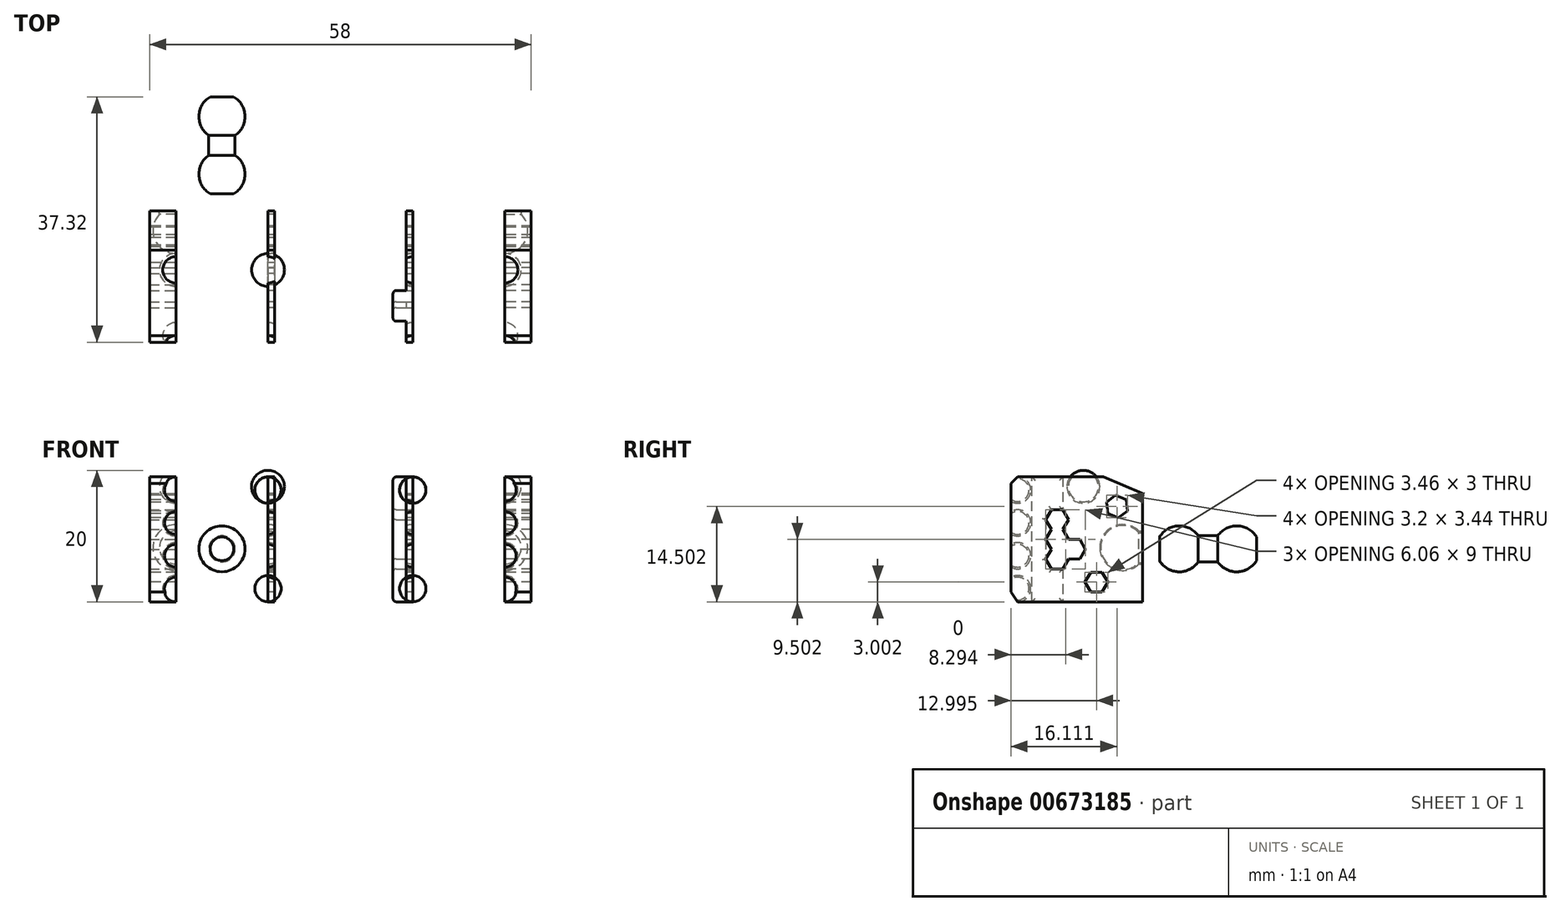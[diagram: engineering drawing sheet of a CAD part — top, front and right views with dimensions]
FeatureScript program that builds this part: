
annotation { "Feature Type Name" : "Feature", "Feature Type Description" : "" }
export const myFeature = defineFeature(function(context is Context, id is Id, definition is map)
    precondition{}
    {
        {
            var Q0;
            Q0=qCreatedBy(makeId("Right.planeOp"),FACE);
            var sketch = newSketch(context, id + "F0", { "sketchPlane" : qUnion([Q0])});
            skPoint(sketch, "E0.startSnap0", {"position": v(7.18, 6.6) * mm});
            skLineSegment(sketch, "E1", {"start": v(7.18, -0.9) * mm, "end": v(-7.82, -0.9) * mm});
            skLineSegment(sketch, "E2", {"start": v(-0.32, 14.1) * mm, "end": v(-0.32, 15.6) * mm, "construction": true});
            skPoint(sketch, "E2.endSnap0", {"position": v(-0.32, 14.1) * mm});
            skLineSegment(sketch, "E3", {"start": v(-4.07, 15.6) * mm, "end": v(-4.27, 15.6) * mm});
            skLineSegment(sketch, "E4", {"start": v(-7.82, 15.6) * mm, "end": v(-7.82, -0.9) * mm});
            skPoint(sketch, "E5.centerSnap0", {"position": v(-4.07, 15.6) * mm});
            skLineSegment(sketch, "E6.bottom", {"start": v(-7.82, 15.6) * mm, "end": v(-12.82, 15.6) * mm});
            skLineSegment(sketch, "E6.top", {"start": v(-7.82, -0.9) * mm, "end": v(-12.82, -0.9) * mm});
            skLineSegment(sketch, "E6.right", {"start": v(-12.82, 15.6) * mm, "end": v(-12.82, -0.9) * mm});
            skArc(sketch, "E7", {"start": v(-13.82, 14.6) * mm, "mid": v(-11.82, 12.6) * mm, "end": v(-9.82, 14.6) * mm});
            skArc(sketch, "E8.1.0.0", {"start": v(-13.82, 9.6) * mm, "mid": v(-11.82, 7.6) * mm, "end": v(-9.82, 9.6) * mm});
            skArc(sketch, "E8.2.0.0", {"start": v(-13.82, 4.6) * mm, "mid": v(-11.82, 2.6) * mm, "end": v(-9.82, 4.6) * mm});
            skArc(sketch, "E8.3.0.0", {"start": v(-13.82, -0.4) * mm, "mid": v(-11.82, -2.4) * mm, "end": v(-9.82, -0.4) * mm});
            skLineSegment(sketch, "E8.direction1", {"start": v(-11.82, 14.6) * mm, "end": v(-11.82, 9.6) * mm, "construction": true});
            skArc(sketch, "E9", {"start": v(-4.32, 15.1) * mm, "mid": v(-1.82, 12.6) * mm, "end": v(0.68, 15.1) * mm});
            skLineSegment(sketch, "E10", {"start": v(-11.82, -2.4) * mm, "end": v(7.18, -2.4) * mm});
            skLineSegment(sketch, "E11", {"start": v(-11.82, 16.6) * mm, "end": v(1.18, 16.6) * mm});
            skLineSegment(sketch, "E12", {"start": v(1.18, 16.6) * mm, "end": v(7.18, 14.1) * mm});
            skLineSegment(sketch, "E13", {"start": v(7.18, 14.1) * mm, "end": v(7.18, -2.4) * mm});
            skLineSegment(sketch, "E14", {"start": v(-12.82, -0.9) * mm, "end": v(-11.82, -2.4) * mm});
            skLineSegment(sketch, "E15", {"start": v(-11.82, 16.6) * mm, "end": v(-12.82, 15.6) * mm});
            skLineSegment(sketch, "E16", {"start": v(-13.82, -0.4) * mm, "end": v(-9.82, -0.4) * mm});
            skLineSegment(sketch, "E17", {"start": v(-9.82, 4.6) * mm, "end": v(-13.82, 4.6) * mm});
            skLineSegment(sketch, "E18", {"start": v(-9.82, 9.6) * mm, "end": v(-13.82, 9.6) * mm});
            skLineSegment(sketch, "E19", {"start": v(-9.82, 14.6) * mm, "end": v(-13.82, 14.6) * mm});
            skLineSegment(sketch, "E20", {"start": v(0.68, 15.1) * mm, "end": v(-4.32, 15.1) * mm});
            skArc(sketch, "E21", {"start": v(0.68, 5.85) * mm, "mid": v(2.82, 2.62) * mm, "end": v(6.62, 3.35) * mm});
            skPoint(sketch, "E21.centerSnap0", {"position": v(7.18, 5.85) * mm});
            skLineSegment(sketch, "E22", {"start": v(0.68, 5.85) * mm, "end": v(7.68, 5.85) * mm});
            skLineSegment(sketch, "E23", {"start": v(7.68, 5.85) * mm, "end": v(7.68, 3.35) * mm, "construction": true});
            skLineSegment(sketch, "E24", {"start": v(7.18, 3.35) * mm, "end": v(6.62, 3.35) * mm});
            skSolve(sketch);
        }
        {
            var Q0;
            {var subQ0=sQuery(id+"F0.wireOp",EDGE,"E8.1.0.0");var subQ1=sQuery(id+"F0.wireOp",EDGE,"E6.right");var subQ2=makeQuery(id+"F0.imprint","INTERSECT",VERTEX,{"disambiguationData":[OD(0.0)],"derivedFrom":[subQ1,subQ0]});Q0=makeQuery(id+"F0.imprint","IMPRINT",FACE,{"disambiguationData":[TD([[makeQuery(id+"F0.imprint","IMPRINT",EDGE,{"disambiguationData":[TD([[subQ2,-1.0]])],"derivedFrom":subQ1}),1.0]])]});}
            var Q1;
            {var subQ0=sQuery(id+"F0.wireOp",EDGE,"E8.2.0.0");var subQ1=sQuery(id+"F0.wireOp",EDGE,"E6.right");var subQ2=makeQuery(id+"F0.imprint","INTERSECT",VERTEX,{"disambiguationData":[OD(0.0)],"derivedFrom":[subQ1,subQ0]});Q1=makeQuery(id+"F0.imprint","IMPRINT",FACE,{"disambiguationData":[TD([[makeQuery(id+"F0.imprint","IMPRINT",EDGE,{"disambiguationData":[TD([[subQ2,-1.0]])],"derivedFrom":subQ1}),1.0]])]});}
            var Q2;
            {var subQ0=sQuery(id+"F0.wireOp",EDGE,"E9");var subQ1=makeQuery(id+"F0.imprint","IMPRINT",VERTEX,{"derivedFrom":subQ0});Q2=makeQuery(id+"F0.imprint","IMPRINT",FACE,{"disambiguationData":[TD([[makeQuery(id+"F0.imprint","IMPRINT",EDGE,{"disambiguationData":[TD([[subQ1,1.0]])],"derivedFrom":subQ0}),1.0]])]});}
            var Q3;
            {var subQ5=sQuery(id+"F0.wireOp",EDGE,"E1");Q3=makeQuery(id+"F0.imprint","IMPRINT",FACE,{"disambiguationData":[TD([[makeQuery(id+"F0.imprint","IMPRINT",EDGE,{"derivedFrom":subQ5}),1.0]])]});}
            var Q4;
            {var subQ0=sQuery(id+"F0.wireOp",EDGE,"E6.right");var subQ3=sQuery(id+"F0.wireOp",EDGE,"E7");var subQ5=makeQuery(id+"F0.imprint","INTERSECT",VERTEX,{"derivedFrom":[subQ0,subQ3]});Q4=makeQuery(id+"F0.imprint","IMPRINT",FACE,{"disambiguationData":[TD([[makeQuery(id+"F0.imprint","IMPRINT",EDGE,{"disambiguationData":[TD([[subQ5,-1.0]])],"derivedFrom":subQ3}),1.0]])]});}
            var Q5;
            {var subQ0=sQuery(id+"F0.wireOp",EDGE,"E15");Q5=makeQuery(id+"F0.imprint","IMPRINT",FACE,{"disambiguationData":[TD([[makeQuery(id+"F0.imprint","IMPRINT",EDGE,{"derivedFrom":subQ0}),1.0]])]});}
            var Q6;
            {var subQ0=sQuery(id+"F0.wireOp",EDGE,"E6.right");var subQ3=sQuery(id+"F0.wireOp",EDGE,"E8.3.0.0");var subQ5=makeQuery(id+"F0.imprint","INTERSECT",VERTEX,{"derivedFrom":[subQ0,subQ3]});Q6=makeQuery(id+"F0.imprint","IMPRINT",FACE,{"disambiguationData":[TD([[makeQuery(id+"F0.imprint","IMPRINT",EDGE,{"disambiguationData":[TD([[subQ5,1.0]])],"derivedFrom":subQ3}),1.0]])]});}
            var Q7;
            {var subQ0=sQuery(id+"F0.wireOp",EDGE,"E14");Q7=makeQuery(id+"F0.imprint","IMPRINT",FACE,{"disambiguationData":[TD([[makeQuery(id+"F0.imprint","IMPRINT",EDGE,{"derivedFrom":subQ0}),1.0]])]});}
            var Q8;
            {var subQ9=sQuery(id+"F0.wireOp",EDGE,"E1");Q8=makeQuery(id+"F0.imprint","IMPRINT",FACE,{"disambiguationData":[TD([[makeQuery(id+"F0.imprint","IMPRINT",EDGE,{"derivedFrom":subQ9}),-1.0]])]});}
            var Q9;
            {var subQ5=sQuery(id+"F0.wireOp",EDGE,"E4");Q9=makeQuery(id+"F0.imprint","IMPRINT",FACE,{"disambiguationData":[TD([[makeQuery(id+"F0.imprint","IMPRINT",EDGE,{"derivedFrom":subQ5}),-1.0]])]});}
            var Q10;
            {var subQ0=sQuery(id+"F0.wireOp",EDGE,"E18");var subQ1=sQuery(id+"F0.wireOp",EDGE,"E6.right");var subQ2=makeQuery(id+"F0.imprint","INTERSECT",VERTEX,{"derivedFrom":[subQ1,subQ0]});Q10=makeQuery(id+"F0.imprint","IMPRINT",FACE,{"disambiguationData":[TD([[makeQuery(id+"F0.imprint","IMPRINT",EDGE,{"disambiguationData":[TD([[subQ2,-1.0]])],"derivedFrom":subQ1}),1.0]])]});}
            var Q11;
            {var subQ0=sQuery(id+"F0.wireOp",EDGE,"E17");var subQ1=sQuery(id+"F0.wireOp",EDGE,"E6.right");var subQ2=makeQuery(id+"F0.imprint","INTERSECT",VERTEX,{"derivedFrom":[subQ1,subQ0]});Q11=makeQuery(id+"F0.imprint","IMPRINT",FACE,{"disambiguationData":[TD([[makeQuery(id+"F0.imprint","IMPRINT",EDGE,{"disambiguationData":[TD([[subQ2,-1.0]])],"derivedFrom":subQ1}),1.0]])]});}
            var Q12;
            Q12=makeQuery(id+"F0.imprint","IMPRINT",FACE,{"disambiguationData":[TD([[makeQuery(id+"F0.imprint","IMPRINT",EDGE,{"derivedFrom":sQuery(id+"F0.wireOp",EDGE,"E9")}),1.0]])]});
            var Q13;
            {var subQ3=sQuery(id+"F0.wireOp",EDGE,"E8.3.0.0");var subQ5=sQuery(id+"F0.wireOp",EDGE,"E16");var subQ7=makeQuery(id+"F0.imprint","INTERSECT",VERTEX,{"disambiguationData":[OD(1.0)],"derivedFrom":[subQ3,subQ5]});Q13=makeQuery(id+"F0.imprint","IMPRINT",FACE,{"disambiguationData":[TD([[makeQuery(id+"F0.imprint","IMPRINT",EDGE,{"disambiguationData":[TD([[subQ7,1.0]])],"derivedFrom":subQ3}),1.0]])]});}
            var Q14;
            {var subQ4=sQuery(id+"F0.wireOp",EDGE,"E21");Q14=makeQuery(id+"F0.imprint","IMPRINT",FACE,{"disambiguationData":[TD([[makeQuery(id+"F0.imprint","IMPRINT",EDGE,{"derivedFrom":subQ4}),1.0]])]});}
            extrude(context, id + "F1", {"entities" : qUnion([Q0, Q1, Q2, Q3, Q4, Q5, Q6, Q7, Q8, Q9, Q10, Q11, Q12, Q13, Q14]), "oppositeDirection" : true, "depth" : 4 * mm});
        }
        {
            var Q0;
            {var subQ0=sQuery(id+"F0.wireOp",EDGE,"E14");Q0=makeQuery(id+"F0.imprint","IMPRINT",FACE,{"disambiguationData":[TD([[makeQuery(id+"F0.imprint","IMPRINT",EDGE,{"derivedFrom":subQ0}),1.0]])]});}
            var Q1;
            {var subQ0=sQuery(id+"F0.wireOp",EDGE,"E14");Q1=makeQuery(id+"F0.imprint","IMPRINT",FACE,{"disambiguationData":[TD([[makeQuery(id+"F0.imprint","IMPRINT",EDGE,{"derivedFrom":subQ0}),-1.0]])]});}
            var Q2;
            {var subQ3=sQuery(id+"F0.wireOp",EDGE,"E8.3.0.0");var subQ5=sQuery(id+"F0.wireOp",EDGE,"E16");var subQ7=makeQuery(id+"F0.imprint","INTERSECT",VERTEX,{"disambiguationData":[OD(1.0)],"derivedFrom":[subQ3,subQ5]});Q2=makeQuery(id+"F0.imprint","IMPRINT",FACE,{"disambiguationData":[TD([[makeQuery(id+"F0.imprint","IMPRINT",EDGE,{"disambiguationData":[TD([[subQ7,1.0]])],"derivedFrom":subQ3}),1.0]])]});}
            var Q3;
            Q3=sQuery(id+"F0.wireOp",EDGE,"E16");
            revolve(context, id + "F2", {"operationType" : NewBodyOperationType.REMOVE, "entities" : qUnion([Q0, Q1, Q2]), "axis" : qUnion([Q3]), "revolveType" : RevolveType.FULL, "oppositeDirection" : true});
        }
        {
            var Q0;
            {var subQ0=sQuery(id+"F0.wireOp",EDGE,"E17");var subQ1=sQuery(id+"F0.wireOp",EDGE,"E6.right");var subQ2=makeQuery(id+"F0.imprint","INTERSECT",VERTEX,{"derivedFrom":[subQ1,subQ0]});Q0=makeQuery(id+"F0.imprint","IMPRINT",FACE,{"disambiguationData":[TD([[makeQuery(id+"F0.imprint","IMPRINT",EDGE,{"disambiguationData":[TD([[subQ2,-1.0]])],"derivedFrom":subQ1}),1.0]])]});}
            var Q1;
            {var subQ0=sQuery(id+"F0.wireOp",EDGE,"E17");var subQ1=sQuery(id+"F0.wireOp",EDGE,"E6.right");var subQ2=makeQuery(id+"F0.imprint","INTERSECT",VERTEX,{"derivedFrom":[subQ1,subQ0]});Q1=makeQuery(id+"F0.imprint","IMPRINT",FACE,{"disambiguationData":[TD([[makeQuery(id+"F0.imprint","IMPRINT",EDGE,{"disambiguationData":[TD([[subQ2,-1.0]])],"derivedFrom":subQ1}),-1.0]])]});}
            var Q2;
            Q2=sQuery(id+"F0.wireOp",EDGE,"E17");
            revolve(context, id + "F3", {"operationType" : NewBodyOperationType.REMOVE, "entities" : qUnion([Q0, Q1]), "axis" : qUnion([Q2]), "revolveType" : RevolveType.FULL, "oppositeDirection" : true});
        }
        {
            var Q0;
            {var subQ0=sQuery(id+"F0.wireOp",EDGE,"E18");var subQ1=sQuery(id+"F0.wireOp",EDGE,"E6.right");var subQ2=makeQuery(id+"F0.imprint","INTERSECT",VERTEX,{"derivedFrom":[subQ1,subQ0]});Q0=makeQuery(id+"F0.imprint","IMPRINT",FACE,{"disambiguationData":[TD([[makeQuery(id+"F0.imprint","IMPRINT",EDGE,{"disambiguationData":[TD([[subQ2,-1.0]])],"derivedFrom":subQ1}),1.0]])]});}
            var Q1;
            {var subQ0=sQuery(id+"F0.wireOp",EDGE,"E18");var subQ1=sQuery(id+"F0.wireOp",EDGE,"E6.right");var subQ2=makeQuery(id+"F0.imprint","INTERSECT",VERTEX,{"derivedFrom":[subQ1,subQ0]});Q1=makeQuery(id+"F0.imprint","IMPRINT",FACE,{"disambiguationData":[TD([[makeQuery(id+"F0.imprint","IMPRINT",EDGE,{"disambiguationData":[TD([[subQ2,-1.0]])],"derivedFrom":subQ1}),-1.0]])]});}
            var Q2;
            Q2=sQuery(id+"F0.wireOp",EDGE,"E18");
            revolve(context, id + "F4", {"operationType" : NewBodyOperationType.REMOVE, "entities" : qUnion([Q0, Q1]), "axis" : qUnion([Q2]), "revolveType" : RevolveType.FULL, "oppositeDirection" : true});
        }
        {
            var Q0;
            {var subQ0=sQuery(id+"F0.wireOp",EDGE,"E19");var subQ1=sQuery(id+"F0.wireOp",EDGE,"E6.right");var subQ2=makeQuery(id+"F0.imprint","INTERSECT",VERTEX,{"derivedFrom":[subQ1,subQ0]});Q0=makeQuery(id+"F0.imprint","IMPRINT",FACE,{"disambiguationData":[TD([[makeQuery(id+"F0.imprint","IMPRINT",EDGE,{"disambiguationData":[TD([[subQ2,-1.0]])],"derivedFrom":subQ1}),1.0]])]});}
            var Q1;
            {var subQ0=sQuery(id+"F0.wireOp",EDGE,"E19");var subQ1=sQuery(id+"F0.wireOp",EDGE,"E6.right");var subQ2=makeQuery(id+"F0.imprint","INTERSECT",VERTEX,{"derivedFrom":[subQ1,subQ0]});Q1=makeQuery(id+"F0.imprint","IMPRINT",FACE,{"disambiguationData":[TD([[makeQuery(id+"F0.imprint","IMPRINT",EDGE,{"disambiguationData":[TD([[subQ2,-1.0]])],"derivedFrom":subQ1}),-1.0]])]});}
            var Q2;
            Q2=sQuery(id+"F0.wireOp",EDGE,"E19");
            revolve(context, id + "F5", {"operationType" : NewBodyOperationType.REMOVE, "entities" : qUnion([Q0, Q1]), "axis" : qUnion([Q2]), "revolveType" : RevolveType.FULL, "oppositeDirection" : true});
        }
        {
            var Q0;
            Q0=makeQuery(id+"F0.imprint","IMPRINT",FACE,{"disambiguationData":[TD([[makeQuery(id+"F0.imprint","IMPRINT",EDGE,{"derivedFrom":sQuery(id+"F0.wireOp",EDGE,"E9")}),1.0]])]});
            var Q1;
            Q1=sQuery(id+"F0.wireOp",EDGE,"E20");
            revolve(context, id + "F6", {"operationType" : NewBodyOperationType.REMOVE, "entities" : qUnion([Q0]), "axis" : qUnion([Q1]), "revolveType" : RevolveType.FULL, "oppositeDirection" : true});
        }
        {
            var Q0;
            {var subQ4=sQuery(id+"F0.wireOp",EDGE,"E21");Q0=makeQuery(id+"F0.imprint","IMPRINT",FACE,{"disambiguationData":[TD([[makeQuery(id+"F0.imprint","IMPRINT",EDGE,{"derivedFrom":subQ4}),1.0]])]});}
            var Q1;
            Q1=sQuery(id+"F0.wireOp",EDGE,"E22");
            revolve(context, id + "F7", {"operationType" : NewBodyOperationType.REMOVE, "entities" : qUnion([Q0]), "axis" : qUnion([Q1]), "revolveType" : RevolveType.FULL, "oppositeDirection" : true});
        }
        {
            var Q0;
            Q0=makeQuery(id+"F1.opExtrude","CAP_FACE",FACE,{"disambiguationData":[OSD([sQuery(id+"F0.wireOp",EDGE,"E6.right"),sQuery(id+"F0.wireOp",EDGE,"E10"),sQuery(id+"F0.wireOp",EDGE,"E11"),sQuery(id+"F0.wireOp",EDGE,"E12"),sQuery(id+"F0.wireOp",EDGE,"E13"),sQuery(id+"F0.wireOp",EDGE,"E14"),sQuery(id+"F0.wireOp",EDGE,"E15")])],"isStart":true});
            var sketch = newSketch(context, id + "F8", { "sketchPlane" : qUnion([Q0])});
            skCircle(sketch, "E25.cCircle", {"center": v(-5.82, 10.1) * mm, "radius": 1.5 * mm, "construction": true});
            skLineSegment(sketch, "E25.0", {"start": v(-4.96, 8.6) * mm, "end": v(-6.7, 8.6) * mm});
            skLineSegment(sketch, "E25.1", {"start": v(-6.7, 8.6) * mm, "end": v(-7.56, 10.1) * mm});
            skLineSegment(sketch, "E25.2", {"start": v(-7.56, 10.1) * mm, "end": v(-6.7, 11.6) * mm});
            skLineSegment(sketch, "E25.3", {"start": v(-6.7, 11.6) * mm, "end": v(-4.96, 11.6) * mm});
            skLineSegment(sketch, "E25.4", {"start": v(-4.96, 11.6) * mm, "end": v(-4.1, 10.1) * mm});
            skLineSegment(sketch, "E25.5", {"start": v(-4.1, 10.1) * mm, "end": v(-4.96, 8.6) * mm});
            skPoint(sketch, "E25.0.midPoint", {"position": v(-5.82, 8.6) * mm});
            skCircle(sketch, "E26.cCircle", {"center": v(-5.82, 7.1) * mm, "radius": 1.5 * mm, "construction": true});
            skLineSegment(sketch, "E26.0", {"start": v(-4.96, 5.6) * mm, "end": v(-6.7, 5.6) * mm});
            skLineSegment(sketch, "E26.1", {"start": v(-6.7, 5.6) * mm, "end": v(-7.56, 7.1) * mm});
            skLineSegment(sketch, "E26.2", {"start": v(-7.56, 7.1) * mm, "end": v(-6.7, 8.6) * mm});
            skLineSegment(sketch, "E26.3", {"start": v(-6.7, 8.6) * mm, "end": v(-4.96, 8.6) * mm});
            skLineSegment(sketch, "E26.4", {"start": v(-4.96, 8.6) * mm, "end": v(-4.1, 7.1) * mm});
            skLineSegment(sketch, "E26.5", {"start": v(-4.1, 7.1) * mm, "end": v(-4.96, 5.6) * mm});
            skPoint(sketch, "E26.0.midPoint", {"position": v(-5.82, 5.6) * mm});
            skCircle(sketch, "E27.cCircle", {"center": v(-5.82, 4.1) * mm, "radius": 1.5 * mm, "construction": true});
            skLineSegment(sketch, "E27.0", {"start": v(-4.96, 2.6) * mm, "end": v(-6.7, 2.6) * mm});
            skLineSegment(sketch, "E27.1", {"start": v(-6.7, 2.6) * mm, "end": v(-7.56, 4.1) * mm});
            skLineSegment(sketch, "E27.2", {"start": v(-7.56, 4.1) * mm, "end": v(-6.7, 5.6) * mm});
            skLineSegment(sketch, "E27.3", {"start": v(-6.7, 5.6) * mm, "end": v(-4.96, 5.6) * mm});
            skLineSegment(sketch, "E27.4", {"start": v(-4.96, 5.6) * mm, "end": v(-4.1, 4.1) * mm});
            skLineSegment(sketch, "E27.5", {"start": v(-4.1, 4.1) * mm, "end": v(-4.96, 2.6) * mm});
            skPoint(sketch, "E27.0.midPoint", {"position": v(-5.82, 2.6) * mm});
            skCircle(sketch, "E28.cCircle", {"center": v(-3.23, 8.6) * mm, "radius": 1.5 * mm, "construction": true});
            skLineSegment(sketch, "E28.0", {"start": v(-2.36, 7.1) * mm, "end": v(-4.1, 7.1) * mm});
            skLineSegment(sketch, "E28.1", {"start": v(-4.1, 7.1) * mm, "end": v(-4.96, 8.6) * mm});
            skLineSegment(sketch, "E28.2", {"start": v(-4.96, 8.6) * mm, "end": v(-4.1, 10.1) * mm});
            skLineSegment(sketch, "E28.3", {"start": v(-4.1, 10.1) * mm, "end": v(-2.36, 10.1) * mm});
            skLineSegment(sketch, "E28.4", {"start": v(-2.36, 10.1) * mm, "end": v(-1.5, 8.6) * mm});
            skLineSegment(sketch, "E28.5", {"start": v(-1.5, 8.6) * mm, "end": v(-2.36, 7.1) * mm});
            skPoint(sketch, "E28.0.midPoint", {"position": v(-3.23, 7.1) * mm});
            skCircle(sketch, "E29.cCircle", {"center": v(-3.23, 5.6) * mm, "radius": 1.5 * mm, "construction": true});
            skLineSegment(sketch, "E29.0", {"start": v(-2.36, 4.1) * mm, "end": v(-4.1, 4.1) * mm});
            skLineSegment(sketch, "E29.1", {"start": v(-4.1, 4.1) * mm, "end": v(-4.96, 5.6) * mm});
            skLineSegment(sketch, "E29.2", {"start": v(-4.96, 5.6) * mm, "end": v(-4.1, 7.1) * mm});
            skLineSegment(sketch, "E29.3", {"start": v(-4.1, 7.1) * mm, "end": v(-2.36, 7.1) * mm});
            skLineSegment(sketch, "E29.4", {"start": v(-2.36, 7.1) * mm, "end": v(-1.5, 5.6) * mm});
            skLineSegment(sketch, "E29.5", {"start": v(-1.5, 5.6) * mm, "end": v(-2.36, 4.1) * mm});
            skPoint(sketch, "E29.0.midPoint", {"position": v(-3.23, 4.1) * mm});
            skSolve(sketch);
        }
        {
            var Q0;
            Q0=makeQuery(id+"F8.imprint","IMPRINT",FACE,{"disambiguationData":[TD([[makeQuery(id+"F8.imprint","IMPRINT",EDGE,{"derivedFrom":sQuery(id+"F8.wireOp",EDGE,"E26.1")}),-1.0]])]});
            var Q1;
            Q1=makeQuery(id+"F8.imprint","IMPRINT",FACE,{"disambiguationData":[TD([[makeQuery(id+"F8.imprint","IMPRINT",EDGE,{"derivedFrom":sQuery(id+"F8.wireOp",EDGE,"E28.1")}),-1.0]])]});
            var Q2;
            Q2=makeQuery(id+"F8.imprint","IMPRINT",FACE,{"disambiguationData":[TD([[makeQuery(id+"F8.imprint","IMPRINT",EDGE,{"derivedFrom":sQuery(id+"F8.wireOp",EDGE,"E29.0")}),-1.0]])]});
            var Q3;
            Q3=makeQuery(id+"F8.imprint","IMPRINT",FACE,{"disambiguationData":[TD([[makeQuery(id+"F8.imprint","IMPRINT",EDGE,{"derivedFrom":sQuery(id+"F8.wireOp",EDGE,"E25.1")}),-1.0]])]});
            var Q4;
            Q4=makeQuery(id+"F8.imprint","IMPRINT",FACE,{"disambiguationData":[TD([[makeQuery(id+"F8.imprint","IMPRINT",EDGE,{"derivedFrom":sQuery(id+"F8.wireOp",EDGE,"E27.0")}),-1.0]])]});
            extrude(context, id + "F9", {"entities" : qUnion([Q0, Q1, Q2, Q3, Q4]), "operationType" : NewBodyOperationType.REMOVE, "oppositeDirection" : true, "depth" : 6.9 * mm});
        }
        {
            var Q0;
            Q0=qCreatedBy(makeId("Right.planeOp"),FACE);
            cPlane(context, id + "F10", {"entities" : qUnion([Q0]), "cplaneType" : CPlaneType.OFFSET, "offset" : 7 * mm, "width" : 150 * mm, "height" : 150 * mm});
        }
        {
            var Q0;
            Q0=makeQuery(id+"F1.opExtrude","SWEPT_BODY",BODY,{"disambiguationData":[OSD([sQuery(id+"F0.wireOp",EDGE,"E6.right"),sQuery(id+"F0.wireOp",EDGE,"E10"),sQuery(id+"F0.wireOp",EDGE,"E11"),sQuery(id+"F0.wireOp",EDGE,"E12"),sQuery(id+"F0.wireOp",EDGE,"E13"),sQuery(id+"F0.wireOp",EDGE,"E14"),sQuery(id+"F0.wireOp",EDGE,"E15")])]});
            var Q1;
            Q1=qCreatedBy(id+"F10.planeOp",FACE);
            mirror(context, id + "F11", {"entities" : qUnion([Q0]), "mirrorPlane" : qUnion([Q1])});
        }
        {
            var Q0;
            Q0=makeQuery(id+"F11.opPattern","COPY",FACE,{"derivedFrom":makeQuery(id+"F1.opExtrude","CAP_FACE",FACE,{"disambiguationData":[OSD([sQuery(id+"F0.wireOp",EDGE,"E6.right"),sQuery(id+"F0.wireOp",EDGE,"E10"),sQuery(id+"F0.wireOp",EDGE,"E11"),sQuery(id+"F0.wireOp",EDGE,"E12"),sQuery(id+"F0.wireOp",EDGE,"E13"),sQuery(id+"F0.wireOp",EDGE,"E14"),sQuery(id+"F0.wireOp",EDGE,"E15")])],"isStart":false}),"instanceName":"1"});
            extrude(context, id + "F12", {"entities" : qUnion([Q0]), "operationType" : NewBodyOperationType.REMOVE, "oppositeDirection" : true, "depth" : 3 * mm});
        }
        {
            var Q0;
            Q0=qCreatedBy(id+"F10.planeOp",FACE);
            var sketch = newSketch(context, id + "F13", { "sketchPlane" : qUnion([Q0])});
            skArc(sketch, "E30", {"start": v(15.62, 7.66) * mm, "mid": v(12.63, 9.16) * mm, "end": v(9.75, 7.46) * mm});
            skArc(sketch, "E31", {"start": v(24.5, 7.46) * mm, "mid": v(21.61, 9.16) * mm, "end": v(18.62, 7.66) * mm});
            skLineSegment(sketch, "E32", {"start": v(15.62, 7.66) * mm, "end": v(18.62, 7.66) * mm});
            skLineSegment(sketch, "E33", {"start": v(9.75, 5.66) * mm, "end": v(24.5, 5.66) * mm});
            skLineSegment(sketch, "E34", {"start": v(17.12, 7.66) * mm, "end": v(17.12, 9.42) * mm, "construction": true});
            skLineSegment(sketch, "E35", {"start": v(9.75, 5.66) * mm, "end": v(9.75, 7.46) * mm});
            skPoint(sketch, "E36.start.orphan", {"position": v(9.25, 5.02) * mm});
            skPoint(sketch, "E37.orphan", {"position": v(9.25, 5.66) * mm});
            skLineSegment(sketch, "E38.MirrorCS", {"start": v(24.5, 5.66) * mm, "end": v(24.5, 7.46) * mm});
            skSolve(sketch);
        }
        {
            var Q0;
            Q0=qSketchRegion(id+"F13",true);
            var Q1;
            Q1=sQuery(id+"F13.wireOp",EDGE,"E33");
            revolve(context, id + "F14", {"entities" : qUnion([Q0]), "axis" : qUnion([Q1]), "revolveType" : RevolveType.FULL});
        }
        {
            var Q0;
            Q0=qCreatedBy(makeId("Right.planeOp"),FACE);
            cPlane(context, id + "F15", {"entities" : qUnion([Q0]), "cplaneType" : CPlaneType.OFFSET, "offset" : 25 * mm, "width" : 150 * mm, "height" : 150 * mm});
        }
        {
            var Q0;
            Q0=makeQuery(id+"F1.opExtrude","SWEPT_BODY",BODY,{"disambiguationData":[OSD([sQuery(id+"F0.wireOp",EDGE,"E6.right"),sQuery(id+"F0.wireOp",EDGE,"E10"),sQuery(id+"F0.wireOp",EDGE,"E11"),sQuery(id+"F0.wireOp",EDGE,"E12"),sQuery(id+"F0.wireOp",EDGE,"E13"),sQuery(id+"F0.wireOp",EDGE,"E14"),sQuery(id+"F0.wireOp",EDGE,"E15")])]});
            var Q1;
            Q1=makeQuery(id+"F11.opPattern","COPY",BODY,{"derivedFrom":makeQuery(id+"F1.opExtrude","SWEPT_BODY",BODY,{"disambiguationData":[OSD([sQuery(id+"F0.wireOp",EDGE,"E6.right"),sQuery(id+"F0.wireOp",EDGE,"E10"),sQuery(id+"F0.wireOp",EDGE,"E11"),sQuery(id+"F0.wireOp",EDGE,"E12"),sQuery(id+"F0.wireOp",EDGE,"E13"),sQuery(id+"F0.wireOp",EDGE,"E14"),sQuery(id+"F0.wireOp",EDGE,"E15")])]}),"instanceName":"1"});
            var Q2;
            Q2=qCreatedBy(id+"F15.planeOp",FACE);
            mirror(context, id + "F16", {"entities" : qUnion([Q0, Q1]), "mirrorPlane" : qUnion([Q2])});
        }
        {
            var Q0;
            Q0=makeQuery(id+"F12.boolean.opBoolean","COPY",FACE,{"derivedFrom":makeQuery(id+"F12.opExtrude","CAP_FACE",FACE,{"disambiguationData":[OSD([sQuery(id+"F0.wireOp",EDGE,"E6.right"),sQuery(id+"F0.wireOp",EDGE,"E10"),sQuery(id+"F0.wireOp",EDGE,"E11"),sQuery(id+"F0.wireOp",EDGE,"E12"),sQuery(id+"F0.wireOp",EDGE,"E13"),sQuery(id+"F0.wireOp",EDGE,"E14"),sQuery(id+"F0.wireOp",EDGE,"E15")])],"isStart":false})});
            var sketch = newSketch(context, id + "F17", { "sketchPlane" : qUnion([Q0])});
            skCircle(sketch, "E39.cCircle", {"center": v(3.3, 12.1) * mm, "radius": 1.5 * mm, "construction": true});
            skLineSegment(sketch, "E39.0", {"start": v(3.07, 13.82) * mm, "end": v(4.67, 13.15) * mm});
            skLineSegment(sketch, "E39.1", {"start": v(4.67, 13.15) * mm, "end": v(4.89, 11.44) * mm});
            skLineSegment(sketch, "E39.2", {"start": v(4.89, 11.44) * mm, "end": v(3.51, 10.38) * mm});
            skLineSegment(sketch, "E39.3", {"start": v(3.51, 10.38) * mm, "end": v(1.91, 11.05) * mm});
            skLineSegment(sketch, "E39.4", {"start": v(1.91, 11.05) * mm, "end": v(1.7, 12.77) * mm});
            skLineSegment(sketch, "E39.5", {"start": v(1.7, 12.77) * mm, "end": v(3.07, 13.82) * mm});
            skPoint(sketch, "E39.0.midPoint", {"position": v(3.87, 13.49) * mm});
            skCircle(sketch, "E40.cCircle", {"center": v(0.18, 0.6) * mm, "radius": 1.5 * mm, "construction": true});
            skLineSegment(sketch, "E40.0", {"start": v(1.04, -0.9) * mm, "end": v(-0.7, -0.9) * mm});
            skLineSegment(sketch, "E40.1", {"start": v(-0.7, -0.9) * mm, "end": v(-1.56, 0.6) * mm});
            skLineSegment(sketch, "E40.2", {"start": v(-1.56, 0.6) * mm, "end": v(-0.7, 2.1) * mm});
            skLineSegment(sketch, "E40.3", {"start": v(-0.7, 2.1) * mm, "end": v(1.04, 2.1) * mm});
            skLineSegment(sketch, "E40.4", {"start": v(1.04, 2.1) * mm, "end": v(1.9, 0.6) * mm});
            skLineSegment(sketch, "E40.5", {"start": v(1.9, 0.6) * mm, "end": v(1.04, -0.9) * mm});
            skPoint(sketch, "E40.0.midPoint", {"position": v(0.18, -0.9) * mm});
            skLineSegment(sketch, "E41", {"start": v(7.18, 8.14) * mm, "end": v(7.18, 14.1) * mm});
            skLineSegment(sketch, "E42", {"start": v(7.18, 14.1) * mm, "end": v(1.18, 16.6) * mm});
            skLineSegment(sketch, "E43", {"start": v(-3.56, 12.2) * mm, "end": v(-3.56, 0.83) * mm});
            skLineSegment(sketch, "E44", {"start": v(-3.56, 0.83) * mm, "end": v(-2.32, -2.4) * mm});
            skLineSegment(sketch, "E45", {"start": v(-2.32, -2.4) * mm, "end": v(7.18, -2.4) * mm});
            skLineSegment(sketch, "E46", {"start": v(7.18, -2.4) * mm, "end": v(7.18, 3.56) * mm});
            skLineSegment(sketch, "E47", {"start": v(7.18, 3.56) * mm, "end": v(6.62, 3.56) * mm});
            skLineSegment(sketch, "E48", {"start": v(6.62, 3.56) * mm, "end": v(6.62, 8.14) * mm});
            skArc(sketch, "E49", {"start": v(6.62, 8.14) * mm, "mid": v(0.82, 5.85) * mm, "end": v(6.62, 3.56) * mm});
            skCircle(sketch, "E50", {"center": v(-1.82, 15.1) * mm, "radius": 2.3 * mm});
            skLineSegment(sketch, "E51", {"start": v(-3.56, 12.2) * mm, "end": v(-3.09, 13.19) * mm});
            skLineSegment(sketch, "E52", {"start": v(1.18, 16.6) * mm, "end": v(0.2, 16.2) * mm});
            skSolve(sketch);
        }
        {
            var Q0;
            Q0=makeQuery(id+"F17.imprint","IMPRINT",FACE,{"disambiguationData":[TD([[makeQuery(id+"F17.imprint","IMPRINT",EDGE,{"derivedFrom":sQuery(id+"F17.wireOp",EDGE,"E39.0")}),-1.0]])]});
            var Q1;
            Q1=makeQuery(id+"F17.imprint","IMPRINT",FACE,{"disambiguationData":[TD([[makeQuery(id+"F17.imprint","IMPRINT",EDGE,{"derivedFrom":sQuery(id+"F17.wireOp",EDGE,"E40.0")}),-1.0]])]});
            extrude(context, id + "F18", {"entities" : qUnion([Q0, Q1]), "operationType" : NewBodyOperationType.REMOVE, "endBound" : BoundingType.SYMMETRIC, "depth" : 90 * mm});
        }
        {
            var Q0;
            Q0=makeQuery(id+"F16.opPattern","COPY",FACE,{"derivedFrom":makeQuery(id+"F12.boolean.opBoolean","COPY",FACE,{"derivedFrom":makeQuery(id+"F12.opExtrude","CAP_FACE",FACE,{"disambiguationData":[OSD([sQuery(id+"F0.wireOp",EDGE,"E6.right"),sQuery(id+"F0.wireOp",EDGE,"E10"),sQuery(id+"F0.wireOp",EDGE,"E11"),sQuery(id+"F0.wireOp",EDGE,"E12"),sQuery(id+"F0.wireOp",EDGE,"E13"),sQuery(id+"F0.wireOp",EDGE,"E14"),sQuery(id+"F0.wireOp",EDGE,"E15")])],"isStart":false})}),"instanceName":"1"});
            var sketch = newSketch(context, id + "F19", { "sketchPlane" : qUnion([Q0])});
            skLineSegment(sketch, "E53", {"start": v(4.96, 16.6) * mm, "end": v(4.96, -2.4) * mm});
            skLineSegment(sketch, "E54", {"start": v(7.56, 10.1) * mm, "end": v(7.56, 4.1) * mm});
            skLineSegment(sketch, "E55", {"start": v(9.64, -2.4) * mm, "end": v(9.64, 16.6) * mm});
            skSolve(sketch);
        }
        {
            var Q0;
            {var subQ4=sQuery(id+"F19.wireOp",EDGE,"E55");Q0=makeQuery(id+"F19.imprint","IMPRINT",FACE,{"disambiguationData":[TD([[makeQuery(id+"F19.imprint","IMPRINT",EDGE,{"derivedFrom":subQ4}),1.0]])]});}
            extrude(context, id + "F20", {"entities" : qUnion([Q0]), "operationType" : NewBodyOperationType.ADD, "depth" : 2 * mm});
        }
        {
            var Q0;
            Q0=makeQuery(id+"F20.opExtrude","CAP_FACE",FACE,{"disambiguationData":[OSD([sQuery(id+"F0.wireOp",EDGE,"E6.right"),sQuery(id+"F0.wireOp",EDGE,"E10"),sQuery(id+"F0.wireOp",EDGE,"E11"),sQuery(id+"F0.wireOp",EDGE,"E12"),sQuery(id+"F0.wireOp",EDGE,"E13"),sQuery(id+"F0.wireOp",EDGE,"E14"),sQuery(id+"F0.wireOp",EDGE,"E15"),sQuery(id+"F8.wireOp",EDGE,"E25.2"),sQuery(id+"F8.wireOp",EDGE,"E25.3"),sQuery(id+"F8.wireOp",EDGE,"E27.0"),sQuery(id+"F8.wireOp",EDGE,"E27.1"),sQuery(id+"F19.wireOp",EDGE,"E53"),sQuery(id+"F19.wireOp",EDGE,"E54"),sQuery(id+"F19.wireOp",EDGE,"E55")])],"isStart":false});
            fillet(context, id + "F21", {"entities" : qUnion([Q0]), "radius" : .5 * mm, "tangentPropagation" : true, "allowEdgeOverflow" : false});
        }
    });
